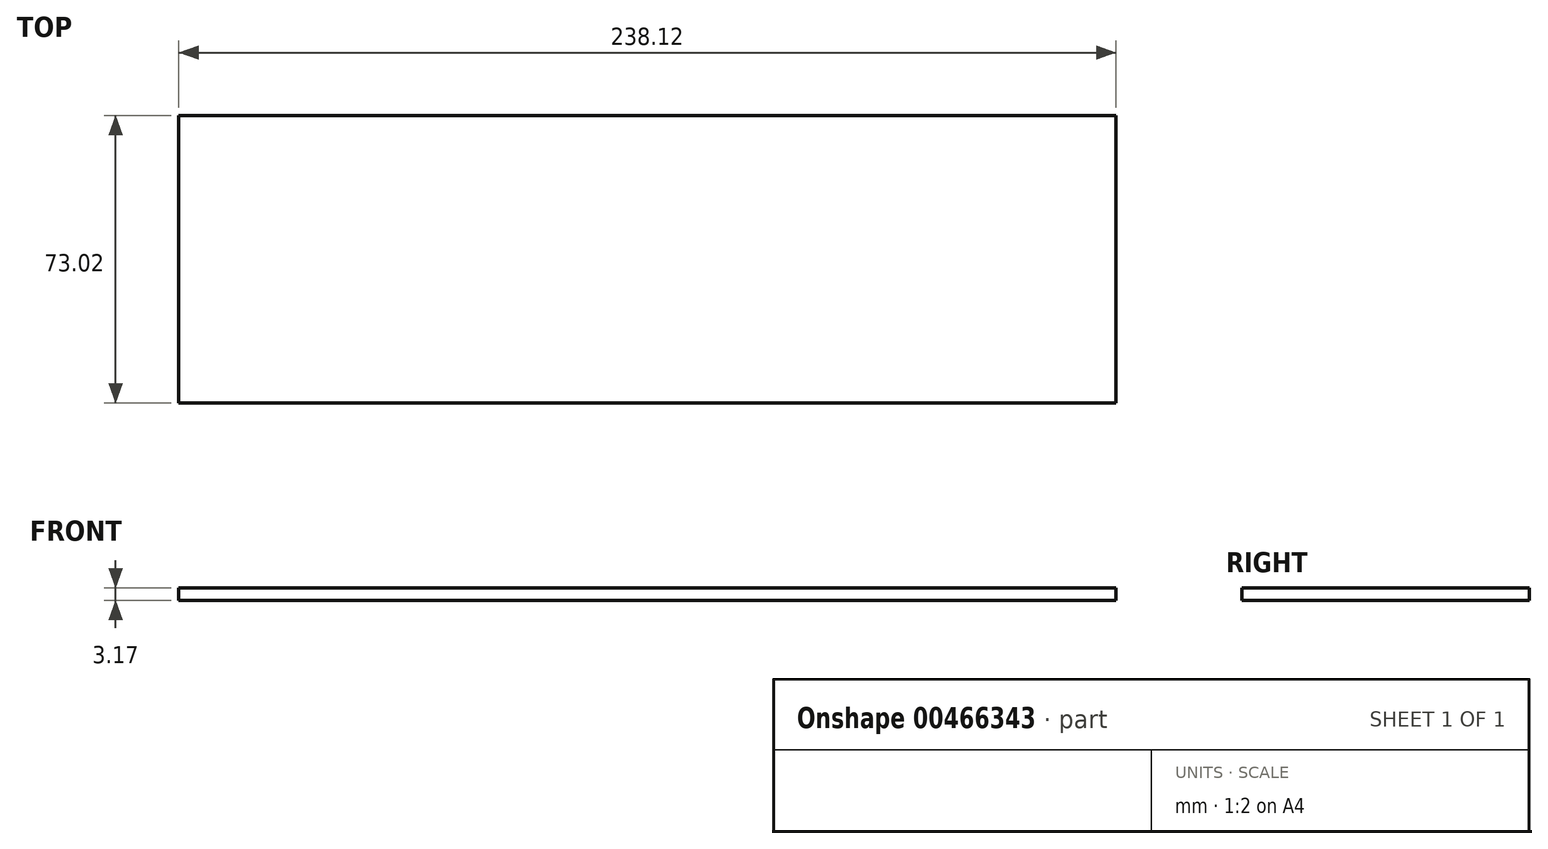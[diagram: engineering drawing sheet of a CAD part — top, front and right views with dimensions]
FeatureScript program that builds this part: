
annotation { "Feature Type Name" : "Feature", "Feature Type Description" : "" }
export const myFeature = defineFeature(function(context is Context, id is Id, definition is map)
    precondition{}
    {
        {
            var Q0;
            Q0=qCreatedBy(makeId("Top.planeOp"),FACE);
            var sketch = newSketch(context, id + "F0", { "sketchPlane" : qUnion([Q0])});
            skLineSegment(sketch, "E0.bottom", {"start": v(-118.03, 32.13) * mm, "end": v(120.1, 32.13) * mm});
            skLineSegment(sketch, "E0.top", {"start": v(-118.03, -40.9) * mm, "end": v(120.1, -40.9) * mm});
            skLineSegment(sketch, "E0.left", {"start": v(-118.03, 32.13) * mm, "end": v(-118.03, -40.9) * mm});
            skLineSegment(sketch, "E0.right", {"start": v(120.1, 32.13) * mm, "end": v(120.1, -40.9) * mm});
            skSolve(sketch);
        }
        {
            var Q0;
            Q0 = qSketchRegion(id + "F0", true);
            extrude(context, id + "F1", {"entities" : qUnion([Q0]), "depth" : 3.17 * mm});
        }
    });
